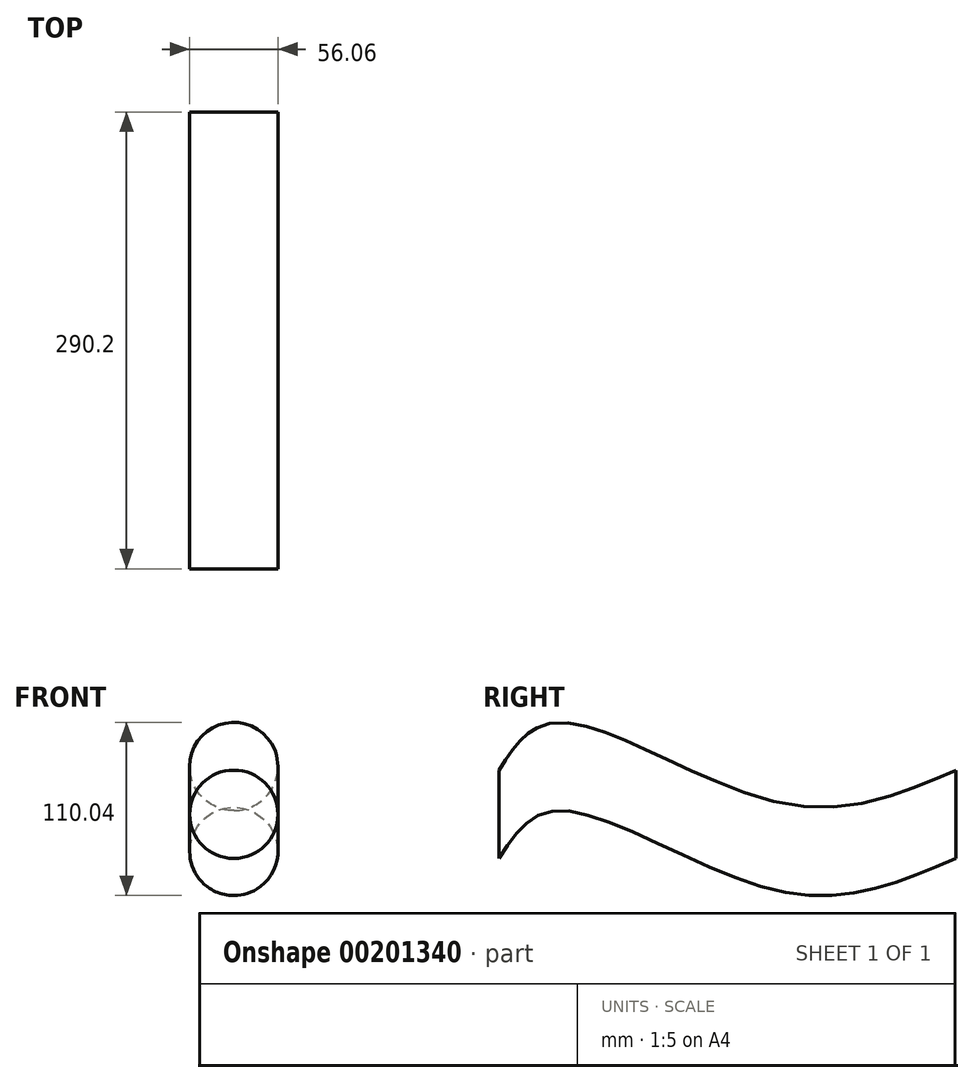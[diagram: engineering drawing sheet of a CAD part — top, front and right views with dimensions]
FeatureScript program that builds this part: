
annotation { "Feature Type Name" : "Feature", "Feature Type Description" : "" }
export const myFeature = defineFeature(function(context is Context, id is Id, definition is map)
    precondition{}
    {
        {
            var Q0;
            Q0=qCreatedBy(makeId("Front.planeOp"),FACE);
            var sketch = newSketch(context, id + "F0", { "sketchPlane" : qUnion([Q0])});
            skCircle(sketch, "E0", {"center": v(0, 0) * mm, "radius": 28.03 * mm});
            skSolve(sketch);
        }
        {
            var Q0;
            Q0=qCreatedBy(makeId("Right.planeOp"),FACE);
            var sketch = newSketch(context, id + "F1", { "sketchPlane" : qUnion([Q0])});
            skFitSpline(sketch, "E1", {"points": [v(0, 0) * mm, v(37.27, 30.35) * mm, v(178.9, -20.87) * mm, v(290.2, 0) * mm], "startDerivative": vector(122.4, 190.73) * mm, "endDerivative": vector(289.02, 125.73) * mm});
            skSolve(sketch);
        }
        {
            var Q0;
            Q0=makeQuery(id+"F0.imprint","IMPRINT",FACE,{"disambiguationData":[TD([[makeQuery(id+"F0.imprint","IMPRINT",EDGE,{"derivedFrom":sQuery(id+"F0.wireOp",EDGE,"E0")}),1.0]])]});
            var Q1;
            Q1=sQuery(id+"F1.wireOp",EDGE,"E1");
            sweep(context, id + "F2", {"profiles" : qUnion([Q0]), "path" : qUnion([Q1]), "keepProfileOrientation" : true});
        }
    });
